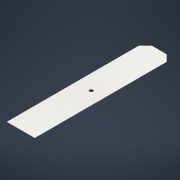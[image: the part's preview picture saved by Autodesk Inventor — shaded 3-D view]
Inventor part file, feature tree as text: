
AUTODESK INVENTOR PART (.ipt)
format: ipt  version: 2022 (Build 260153000, 153)  size: 140,800 bytes
history: native  units: mm
features: other x3, extrude x2, sketch x2, reference x1
ambient origin geometry x8: Origin, YZ Plane, XZ Plane, XY Plane, X Axis, Y Axis, Z Axis, Center Point
bodies: Body1 (feature_tree)
feature tree (8):
  other  "Sólido1"
  extrude  "Extrusión1"  Depth=230.0mm
  extrude  "Extrusion2"  Depth=50.0mm
  sketch  "Boceto1"  dims[d0=1100.0mm d1=230.0mm]
  sketch  "Sketch2"  dims[d2=50.0mm d3=50.0mm d4=50.0mm d5=50.0mm d6=30.0mm d7=100.0mm d10=1.0mm d11=0.0mm d12=30.0mm d13=30.0mm d14=100.0mm d15=275.0mm d16=275.0mm d17=275.0mm d18=100.0mm d19=10.0mm d20=5.0mm d21=50.0mm d22=0.0mm]
  reference  "Reference1"
  other  "Horquilla.iam"
  other  "Horquilla_Cubierta:1"
